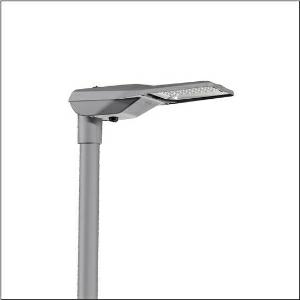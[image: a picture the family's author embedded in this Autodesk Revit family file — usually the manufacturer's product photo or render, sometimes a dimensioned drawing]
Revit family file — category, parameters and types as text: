
# Revit family: streetlight_sl_21_mini___pl52_5xe2h33t08gb_c028
name_source: partatom
category: Lighting Fixtures
units: mm (PartAtom-declared; Revit-internal decimal feet)

## family parameters
Cut with Voids When Loaded = No
Host = Face
Light Source = No
Part Type = Normal
Room Calculation Point = No
Round Connector Dimension = Use Diameter
Shared = No

## types (1)
- --- (1 x LED, 5840 lm, 40.4 W, 3000K)
    Apparent Load = 40 VA
    CIE Flux Codes = 27 59 98 100 100
    Color Rendering = 70
    Color Temperature = 3000K
    Default Elevation = 1800 mm
    Description = Streetlight SL 21 mini, mast luminaire, primary light control with lens, of PMMA, primary optical cover: cover, of toughened safety glass, transparent, light distribution: PL52, light emission: direct distribution, primary light characteristic: asymmetric, installation type: side-entry, post-top, LED, High Power LED, rated luminous flux: 5.840lm, luminous efficacy: 145lm/W, light colour: 730, colour temperature: 3000K, control gear: D4i, control: overheat protection, constant luminous flux control, time-dependent luminous flux control, flexible luminous flux parameterisation, pre-setting: logarithmic dimming characteristic, mains connection: 220..240V, AC, 50/60Hz, start of lifetime: 40W, end of service life: 41W, reduction: 19W, luminaire housing, of diecast aluminium, powder-coated, Siteco® metallic grey (DB 702S), corrosivity category C5 mid according to DIN EN ISO 12944, please order mast flange separately, inclination adjustable: 0°, 5°, 10°, 15°, sealing non-destructively replaceable, multi-level sealing system, length: 628mm, width: 235mm, height: 110mm, mast flange for spigot size: 42mm (side-entry): 5XC10008XM4, 60/48mm (side-entry/post-top): 5XC10108XM2, 76/60mm (side-entry/post-top): 5XC10108XM1, mounting height: 4..8m, Smart Interface below and above, protection rating (complete): IP66, insulation class (complete): insulation class II (safety insulation), certification: CE, ENEC, ENEC+, VDE, impact resistance: IK10, permissible operating ambient temperature for outdoor applications: -40..+50°C, standard-compliant lighting for roads and squares, packaging unit: 1 piece

Light Distribution: PL52
    Height = 110 mm
    Lamp = 1 x LED
    Lamp Light Flux = 5840 lm
    Lamp Power = 40.4 W
    Lamp count = 1
    Length = 625 mm
    Luminous efficacy = 145 lm/W
    Manufacturer = Siteco
    ModVariant = No
    Model = 5XE2H33T08GB
    Number of Poles = 1
    OnlyDefault = Yes
    Power Factor = 1
    Product Name = Streetlight SL 21 mini | PL52
    Product group = mast luminaire | pylon top
    ProductGroupID = 6100
    Protection Class = Protection class II
    Protection Degree = IP 66
    RLX_Detail_Level = 1
    RLX_Emergency_Light_Flux = 0 lm
    RLX_Emergency_Type = 0
    RLX_Emergency_Type_DB = No
    RlxData = <blob elided: 35933 chars, md5=79c7c672>
    Socket = socket
    Standby Power = 0 W
    System Light Flux = 5840 lm
    System Power = 40 W
    Type Comments = factory setting: luminous flux: 100 % | dim-lin: 254 | 812 mA
    Type Image = l_1003514.jpg
    URL = http://relux.com
    VarID = @adj_190056
    Voltage = 0 V
    Weight = 0.00 kg
    Width = 234 mm

## geometry (parser evidence)
native form markers: Blend x4, Sweep x10
no freeform markers — native parametric forms only
